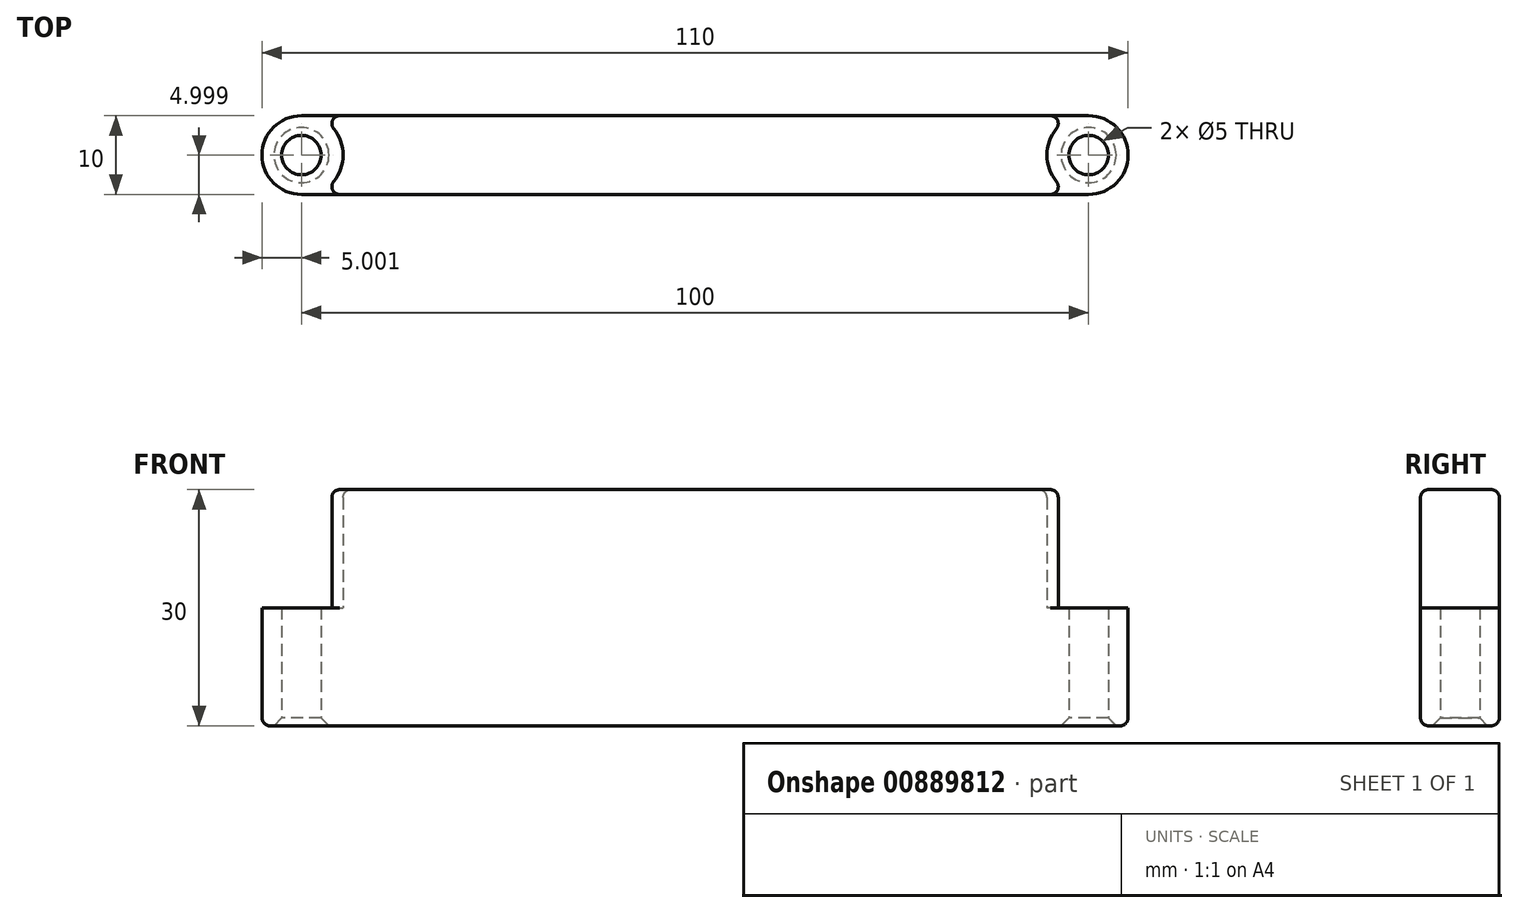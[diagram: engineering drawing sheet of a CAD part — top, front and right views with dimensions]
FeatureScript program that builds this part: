
annotation { "Feature Type Name" : "Feature", "Feature Type Description" : "" }
export const myFeature = defineFeature(function(context is Context, id is Id, definition is map)
    precondition{}
    {
        {
            var Q0;
            Q0=qCreatedBy(makeId("Top.planeOp"),FACE);
            var sketch = newSketch(context, id + "F0", { "sketchPlane" : qUnion([Q0])});
            skLineSegment(sketch, "E0.bottom", {"start": v(-104.3, 20.03) * mm, "end": v(-4.3, 20.03) * mm});
            skLineSegment(sketch, "E0.top", {"start": v(-104.3, 10.03) * mm, "end": v(-4.3, 10.03) * mm});
            skLineSegment(sketch, "E0.left", {"start": v(-104.3, 20.03) * mm, "end": v(-104.3, 10.03) * mm});
            skLineSegment(sketch, "E0.right", {"start": v(-4.3, 20.03) * mm, "end": v(-4.3, 20.03) * mm});
            skArc(sketch, "E1", {"start": v(-104.3, 20.03) * mm, "mid": v(-109.3, 15.03) * mm, "end": v(-104.3, 10.03) * mm});
            skLineSegment(sketch, "E2", {"start": v(-4.3, 20.03) * mm, "end": v(-4.3, 10.03) * mm});
            skLineSegment(sketch, "E3", {"start": v(-4.3, 10.03) * mm, "end": v(-4.3, 10.03) * mm});
            skArc(sketch, "E4", {"start": v(-4.3, 10.03) * mm, "mid": v(0.7, 15.03) * mm, "end": v(-4.3, 20.03) * mm});
            skArc(sketch, "E5.0", {"start": v(-6.06, 20.03) * mm, "mid": v(-9.6, 15.03) * mm, "end": v(-6.06, 10.03) * mm});
            skArc(sketch, "E6.0", {"start": v(-102.54, 10.03) * mm, "mid": v(-99, 15.03) * mm, "end": v(-102.54, 20.03) * mm});
            skCircle(sketch, "E7", {"center": v(-104.3, 15.03) * mm, "radius": 2.5 * mm});
            skCircle(sketch, "E8", {"center": v(-4.3, 15.03) * mm, "radius": 2.5 * mm});
            skSolve(sketch);
        }
        {
            var Q0;
            {var subQ0=sQuery(id+"F0.wireOp",EDGE,"E5.0");Q0=makeQuery(id+"F0.imprint","IMPRINT",FACE,{"disambiguationData":[TD([[makeQuery(id+"F0.imprint","IMPRINT",EDGE,{"derivedFrom":subQ0}),-1.0]])]});}
            extrude(context, id + "F1", {"entities" : qUnion([Q0]), "depth" : 30 * mm, "offsetDistance" : 25 * mm});
        }
        {
            var Q0;
            {var subQ0=sQuery(id+"F0.wireOp",EDGE,"E1");Q0=makeQuery(id+"F0.imprint","IMPRINT",FACE,{"disambiguationData":[TD([[makeQuery(id+"F0.imprint","IMPRINT",EDGE,{"derivedFrom":subQ0}),1.0]])]});}
            var Q1;
            {var subQ9=sQuery(id+"F0.wireOp",EDGE,"E6.0");Q1=makeQuery(id+"F0.imprint","IMPRINT",FACE,{"disambiguationData":[TD([[makeQuery(id+"F0.imprint","IMPRINT",EDGE,{"derivedFrom":subQ9}),1.0]])]});}
            var Q2;
            {var subQ0=sQuery(id+"F0.wireOp",EDGE,"E4");Q2=makeQuery(id+"F0.imprint","IMPRINT",FACE,{"disambiguationData":[TD([[makeQuery(id+"F0.imprint","IMPRINT",EDGE,{"derivedFrom":subQ0}),1.0]])]});}
            var Q3;
            {var subQ8=sQuery(id+"F0.wireOp",EDGE,"E5.0");Q3=makeQuery(id+"F0.imprint","IMPRINT",FACE,{"disambiguationData":[TD([[makeQuery(id+"F0.imprint","IMPRINT",EDGE,{"derivedFrom":subQ8}),1.0]])]});}
            extrude(context, id + "F2", {"entities" : qUnion([Q0, Q1, Q2, Q3]), "operationType" : NewBodyOperationType.ADD, "depth" : 15 * mm, "offsetDistance" : 25 * mm});
        }
        {
            var Q0;
            Q0=makeQuery(id+"F1.opExtrude","SWEPT_EDGE",EDGE,{"disambiguationData":[OSD([sQuery(id+"F0.wireOp",EDGE,"E0.bottom"),sQuery(id+"F0.wireOp",EDGE,"E6.0")])]});
            var Q1;
            Q1=makeQuery(id+"F1.opExtrude","SWEPT_EDGE",EDGE,{"disambiguationData":[OSD([sQuery(id+"F0.wireOp",EDGE,"E0.top"),sQuery(id+"F0.wireOp",EDGE,"E6.0")])]});
            var Q2;
            Q2=makeQuery(id+"F1.opExtrude","SWEPT_EDGE",EDGE,{"disambiguationData":[OSD([sQuery(id+"F0.wireOp",EDGE,"E0.bottom"),sQuery(id+"F0.wireOp",EDGE,"E5.0")])]});
            var Q3;
            Q3=makeQuery(id+"F1.opExtrude","SWEPT_EDGE",EDGE,{"disambiguationData":[OSD([sQuery(id+"F0.wireOp",EDGE,"E0.top"),sQuery(id+"F0.wireOp",EDGE,"E5.0")])]});
            fillet(context, id + "F3", {"entities" : qUnion([Q0, Q1, Q2, Q3]), "radius" : 1 * mm, "tangentPropagation" : true, "allowEdgeOverflow" : false});
        }
        {
            var Q0;
            Q0=makeQuery(id+"F1.opExtrude","CAP_EDGE",EDGE,{"disambiguationData":[OSD([sQuery(id+"F0.wireOp",EDGE,"E0.bottom")])],"isStart":false});
            var Q1;
            {var subQ0=sQuery(id+"F0.wireOp",EDGE,"E0.top");Q1=makeQuery(id+"F2.boolean.opBoolean","MERGE",EDGE,{"derivedFrom":[makeQuery(id+"F1.opExtrude","CAP_EDGE",EDGE,{"disambiguationData":[OSD([subQ0])],"isStart":true}),makeQuery(id+"F2.opExtrude","CAP_EDGE",EDGE,{"disambiguationData":[OSD([subQ0]),TDD([makeQuery(id+"F0.imprint","IMPRINT",EDGE,{"disambiguationData":[TD([[makeQuery(id+"F0.imprint","INTERSECT",VERTEX,{"derivedFrom":[subQ0,sQuery(id+"F0.wireOp",EDGE,"E6.0")]}),1.0]])],"derivedFrom":subQ0})])],"isStart":true}),makeQuery(id+"F2.opExtrude","CAP_EDGE",EDGE,{"disambiguationData":[OSD([subQ0]),TDD([makeQuery(id+"F0.imprint","IMPRINT",EDGE,{"disambiguationData":[TD([[makeQuery(id+"F0.imprint","INTERSECT",VERTEX,{"derivedFrom":[subQ0,sQuery(id+"F0.wireOp",EDGE,"E5.0")]}),-1.0]])],"derivedFrom":subQ0})])],"isStart":true})]});}
            fillet(context, id + "F4", {"entities" : qUnion([Q0, Q1]), "radius" : 1 * mm, "tangentPropagation" : true, "allowEdgeOverflow" : false});
        }
        {
            var Q0;
            Q0=makeQuery(id+"F2.opExtrude","CAP_EDGE",EDGE,{"disambiguationData":[OSD([sQuery(id+"F0.wireOp",EDGE,"E7")])],"isStart":true});
            var Q1;
            Q1=makeQuery(id+"F2.opExtrude","CAP_EDGE",EDGE,{"disambiguationData":[OSD([sQuery(id+"F0.wireOp",EDGE,"E8")])],"isStart":true});
            chamfer(context, id + "F5", {"entities" : qUnion([Q0, Q1]), "width" : 1 * mm, "tangentPropagation" : true});
        }
    });
